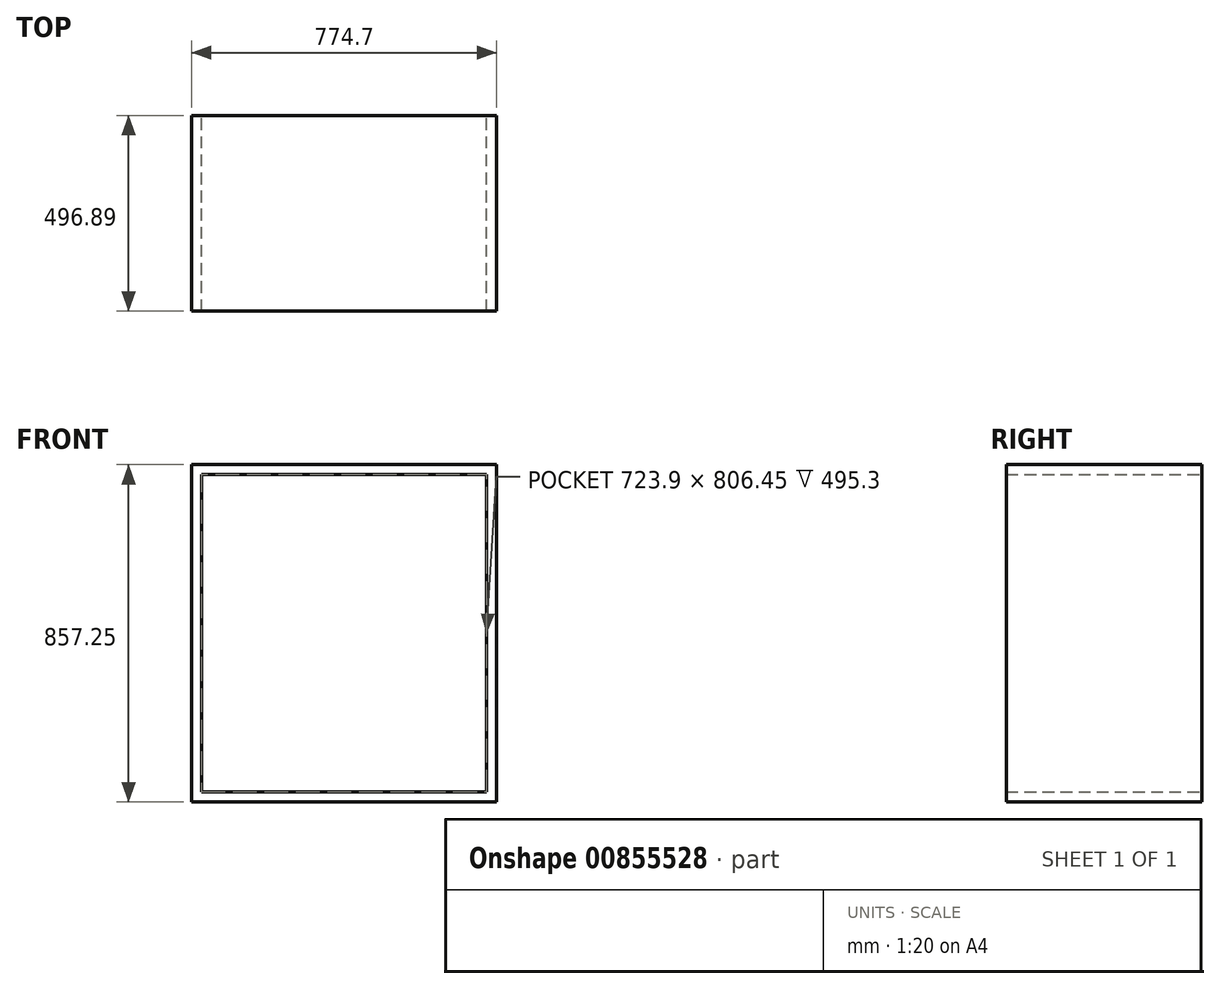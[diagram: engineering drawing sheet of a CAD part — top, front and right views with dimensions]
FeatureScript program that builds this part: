
annotation { "Feature Type Name" : "Feature", "Feature Type Description" : "" }
export const myFeature = defineFeature(function(context is Context, id is Id, definition is map)
    precondition{}
    {
        {
            var Q0;
            Q0=qCreatedBy(makeId("Front.planeOp"),FACE);
            var sketch = newSketch(context, id + "F0", { "sketchPlane" : qUnion([Q0])});
            skLineSegment(sketch, "E0.bottom", {"start": v(-361.25, 478.6) * mm, "end": v(362.65, 478.6) * mm});
            skLineSegment(sketch, "E0.top", {"start": v(-361.25, -327.85) * mm, "end": v(362.65, -327.85) * mm});
            skLineSegment(sketch, "E0.left", {"start": v(-361.25, 478.6) * mm, "end": v(-361.25, -327.85) * mm});
            skLineSegment(sketch, "E0.right", {"start": v(362.65, 478.6) * mm, "end": v(362.65, -327.85) * mm});
            skLineSegment(sketch, "E1.0", {"start": v(-386.65, 504) * mm, "end": v(-386.65, -353.25) * mm});
            skLineSegment(sketch, "E1.1", {"start": v(-386.65, 504) * mm, "end": v(388.05, 504) * mm});
            skLineSegment(sketch, "E1.2", {"start": v(388.05, 504) * mm, "end": v(388.05, -353.25) * mm});
            skLineSegment(sketch, "E1.3", {"start": v(-386.65, -353.25) * mm, "end": v(388.05, -353.25) * mm});
            skSolve(sketch);
        }
        {
            var Q0;
            Q0=makeQuery(id+"F0.imprint","IMPRINT",FACE,{"disambiguationData":[TD([[makeQuery(id+"F0.imprint","IMPRINT",EDGE,{"derivedFrom":sQuery(id+"F0.wireOp",EDGE,"E0.bottom")}),1.0]])]});
            extrude(context, id + "F1", {"entities" : qUnion([Q0]), "depth" : 495.3 * mm, "offsetDistance" : 25.4 * mm});
        }
        {
            var Q0;
            Q0=makeQuery(id+"F1.opExtrude","SWEPT_FACE",FACE,{"disambiguationData":[OSD([sQuery(id+"F0.wireOp",EDGE,"E1.2")])]});
            var sketch = newSketch(context, id + "F2", { "sketchPlane" : qUnion([Q0])});
            skLineSegment(sketch, "E2.bottom", {"start": v(0, 504) * mm, "end": v(1.59, 504) * mm});
            skLineSegment(sketch, "E2.top", {"start": v(0, -353.25) * mm, "end": v(1.59, -353.25) * mm});
            skLineSegment(sketch, "E2.left", {"start": v(0, 504) * mm, "end": v(0, -353.25) * mm});
            skLineSegment(sketch, "E2.right", {"start": v(1.59, 504) * mm, "end": v(1.59, -353.25) * mm});
            skSolve(sketch);
        }
        {
            var Q0;
            Q0 = qSketchRegion(id + "F2", true);
            var Q1;
            Q1=makeQuery(id+"F1.opExtrude","SWEPT_FACE",FACE,{"disambiguationData":[OSD([sQuery(id+"F0.wireOp",EDGE,"E1.0")])]});
            extrude(context, id + "F3", {"entities" : qUnion([Q0]), "operationType" : NewBodyOperationType.ADD, "endBound" : BoundingType.UP_TO_SURFACE, "oppositeDirection" : true, "depth" : 25.4 * mm, "endBoundEntityFace" : qUnion([Q1]), "offsetDistance" : 25.4 * mm});
        }
    });
